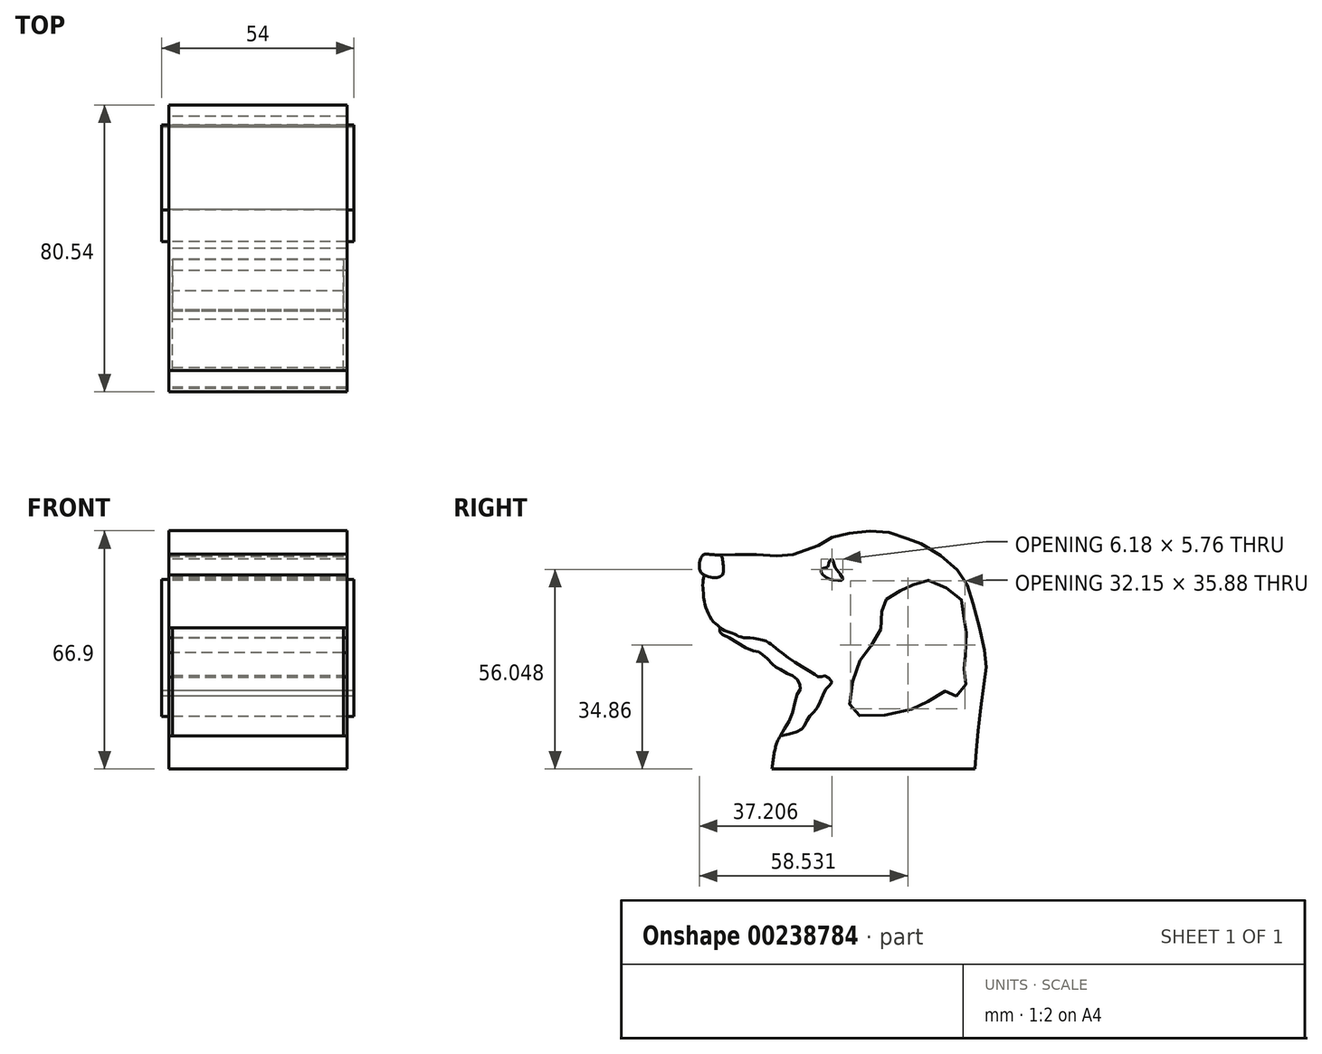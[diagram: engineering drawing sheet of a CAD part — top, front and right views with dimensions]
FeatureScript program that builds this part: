
annotation { "Feature Type Name" : "Feature", "Feature Type Description" : "" }
export const myFeature = defineFeature(function(context is Context, id is Id, definition is map)
    precondition{}
    {
        {
            var Q0;
            Q0=qCreatedBy(makeId("Right.planeOp"),FACE);
            var sketch = newSketch(context, id + "F0", { "sketchPlane" : qUnion([Q0])});
            skFitSpline(sketch, "E0", {"points": [v(-79.8, 68.09) * mm, v(-75.02, 67.83) * mm, v(-71, 68.09) * mm, v(-61.63, 67.75) * mm, v(-57.77, 67.58) * mm, v(-47.3, 71.35) * mm, v(-44.54, 73.11) * mm, v(-37.26, 74.28) * mm, v(-30.64, 74.53) * mm, v(-23.69, 72.44) * mm, v(-20.25, 71.18) * mm, v(-12.22, 66) * mm, v(-7.78, 60.88) * mm, v(-5.52, 54.52) * mm, v(-2.84, 43.97) * mm, v(-1.75, 37.27) * mm, v(-2.25, 32.58) * mm, v(-3.59, 22.36) * mm, v(-4.51, 13.99) * mm, v(-4.93, 7.79) * mm], "startDerivative": vector(114.47, -9.39) * mm, "endDerivative": vector(-6.82, -119.57) * mm});
            skFitSpline(sketch, "E1", {"points": [v(-79.8, 68.09) * mm, v(-81.3, 67.83) * mm, v(-82.28, 64.93) * mm, v(-81.71, 62.82) * mm, v(-81.05, 62.25) * mm, v(-81.27, 60.47) * mm, v(-81.17, 56.98) * mm, v(-80.8, 54.26) * mm, v(-78.37, 49.19) * mm, v(-76.54, 47.5) * mm, v(-76.54, 46.37) * mm, v(-76.08, 45.7) * mm, v(-73.05, 44.19) * mm, v(-68.3, 41.33) * mm, v(-65.83, 40.7) * mm, v(-64.92, 40.14) * mm, v(-62.84, 38.55) * mm, v(-61.08, 36.47) * mm, v(-60.3, 36.16) * mm, v(-57.6, 34.6) * mm, v(-55.62, 33.73) * mm, v(-54.32, 32.1) * mm, v(-53.9, 30.45) * mm, v(-54.84, 28.81) * mm, v(-56.23, 23.43) * mm, v(-58.42, 18.95) * mm, v(-60.61, 14.87) * mm, v(-61.9, 7.79) * mm], "startDerivative": vector(-57.55, 5.23) * mm, "endDerivative": vector(-14.61, -125.43) * mm});
            skLineSegment(sketch, "E2", {"start": v(-61.9, 7.79) * mm, "end": v(-4.93, 7.79) * mm});
            skFitSpline(sketch, "E3", {"points": [v(-10.18, 28.31) * mm, v(-12.3, 29.72) * mm, v(-17.78, 26.97) * mm, v(-23.35, 24.37) * mm, v(-36.44, 22.6) * mm, v(-39.9, 24.93) * mm, v(-38.7, 34.09) * mm, v(-35.74, 40.64) * mm, v(-31.87, 45.5) * mm, v(-31.1, 51.48) * mm, v(-30.88, 53.88) * mm, v(-26.94, 57.6) * mm, v(-24.26, 58.24) * mm, v(-19.83, 60.92) * mm, v(-14.83, 59.44) * mm, v(-8.98, 55.85) * mm, v(-7.92, 49.5) * mm, v(-7.36, 46.41) * mm, v(-7.78, 38.17) * mm, v(-7.92, 35.64) * mm, v(-7.57, 31.2) * mm, v(-10.18, 28.31) * mm]});
            skFitSpline(sketch, "E4", {"points": [v(-76.24, 67.85) * mm, v(-75.82, 66.84) * mm, v(-75.6, 64.92) * mm, v(-75.67, 62.58) * mm, v(-76.77, 61.71) * mm, v(-78.14, 61.51) * mm, v(-81.05, 62.25) * mm], "startDerivative": vector(5.13, -7.92) * mm, "endDerivative": vector(-15.7, 5.75) * mm});
            skFitSpline(sketch, "E5", {"points": [v(-76.54, 47.5) * mm, v(-74.8, 46.47) * mm, v(-72.61, 45.7) * mm, v(-71.45, 45.13) * mm, v(-69.48, 44.64) * mm, v(-68.64, 44.68) * mm, v(-64.27, 43.94) * mm, v(-61.95, 42.63) * mm, v(-59.2, 40.42) * mm], "startDerivative": vector(13.55, -9.33) * mm, "endDerivative": vector(18.65, -15.29) * mm});
            skFitSpline(sketch, "E6", {"points": [v(-48.16, 63.9) * mm, v(-47.75, 62.54) * mm, v(-46.74, 61.72) * mm, v(-45.14, 60.98) * mm, v(-42.03, 60.98) * mm, v(-42.3, 61.86) * mm, v(-42.98, 62.84) * mm, v(-43.93, 63.97) * mm, v(-44.55, 65.65) * mm, v(-45.14, 66.72) * mm, v(-45.97, 65.54) * mm, v(-46.24, 64.5) * mm, v(-48.16, 63.9) * mm]});
            skFitSpline(sketch, "E7", {"points": [v(-59.2, 40.42) * mm, v(-54.35, 36.97) * mm, v(-49.93, 34.35) * mm, v(-48.87, 33.61) * mm, v(-47.61, 33.86) * mm, v(-46.83, 33.86) * mm, v(-45.07, 32.27) * mm, v(-46.2, 30.88) * mm, v(-47.88, 27.81) * mm, v(-49.58, 24.43) * mm, v(-51.55, 22.4) * mm, v(-52.8, 19.88) * mm, v(-54.15, 18.58) * mm, v(-59.59, 17.07) * mm], "startDerivative": vector(40.93, -31.6) * mm, "endDerivative": vector(-58.16, -12.8) * mm});
            skSolve(sketch);
        }
        {
            var Q0;
            {var subQ5=sQuery(id+"F0.wireOp",EDGE,"E0");Q0=makeQuery(id+"F0.imprint","IMPRINT",FACE,{"disambiguationData":[TD([[makeQuery(id+"F0.imprint","IMPRINT",EDGE,{"derivedFrom":subQ5}),-1.0]])]});}
            extrude(context, id + "F1", {"entities" : qUnion([Q0]), "endBound" : BoundingType.SYMMETRIC, "depth" : 50 * mm});
        }
        {
            var Q0;
            Q0=makeQuery(id+"F0.imprint","IMPRINT",FACE,{"disambiguationData":[TD([[makeQuery(id+"F0.imprint","IMPRINT",EDGE,{"derivedFrom":sQuery(id+"F0.wireOp",EDGE,"E3")}),-1.0]])]});
            extrude(context, id + "F2", {"entities" : qUnion([Q0]), "endBound" : BoundingType.SYMMETRIC, "depth" : 54 * mm});
        }
        {
            var Q0;
            Q0=makeQuery(id+"F0.imprint","IMPRINT",FACE,{"disambiguationData":[TD([[makeQuery(id+"F0.imprint","IMPRINT",EDGE,{"derivedFrom":sQuery(id+"F0.wireOp",EDGE,"E6")}),1.0]])]});
            extrude(context, id + "F3", {"entities" : qUnion([Q0]), "endBound" : BoundingType.SYMMETRIC, "depth" : 50 * mm});
        }
        {
            var Q0;
            {var subQ0=sQuery(id+"F0.wireOp",EDGE,"E5");Q0=makeQuery(id+"F0.imprint","IMPRINT",FACE,{"disambiguationData":[TD([[makeQuery(id+"F0.imprint","IMPRINT",EDGE,{"derivedFrom":subQ0}),-1.0]])]});}
            extrude(context, id + "F4", {"entities" : qUnion([Q0]), "endBound" : BoundingType.SYMMETRIC, "depth" : 48 * mm});
        }
        {
            var Q0;
            {var subQ0=sQuery(id+"F0.wireOp",EDGE,"E2");Q0=makeQuery(id+"F0.imprint","IMPRINT",FACE,{"disambiguationData":[TD([[makeQuery(id+"F0.imprint","IMPRINT",EDGE,{"derivedFrom":subQ0}),1.0]])]});}
            extrude(context, id + "F5", {"entities" : qUnion([Q0]), "endBound" : BoundingType.SYMMETRIC, "depth" : 50 * mm});
        }
        {
            var Q0;
            Q0=qCreatedBy(makeId("Top.planeOp"),FACE);
            cPlane(context, id + "F6", {"entities" : qUnion([Q0]), "cplaneType" : CPlaneType.OFFSET, "offset" : 71.5 * mm, "width" : 150 * mm, "height" : 150 * mm});
        }
        {
            var Q0;
            Q0=qCreatedBy(id+"F6.planeOp",FACE);
            var sketch = newSketch(context, id + "F7", { "sketchPlane" : qUnion([Q0])});
            skPoint(sketch, "E8.0", {"position": v(0, -20.25) * mm});
            skPoint(sketch, "E9.0", {"position": v(0, -26.94) * mm});
            skLineSegment(sketch, "E10.0", {"start": v(0, -7.3) * mm, "end": v(0, -40.1) * mm, "construction": true});
            skLineSegment(sketch, "E11", {"start": v(-15, -1.74) * mm, "end": v(15, -1.74) * mm, "construction": true});
            skLineSegment(sketch, "E12", {"start": v(-7.34, -20.25) * mm, "end": v(7.14, -20.25) * mm, "construction": true});
            skSolve(sketch);
        }
    });
